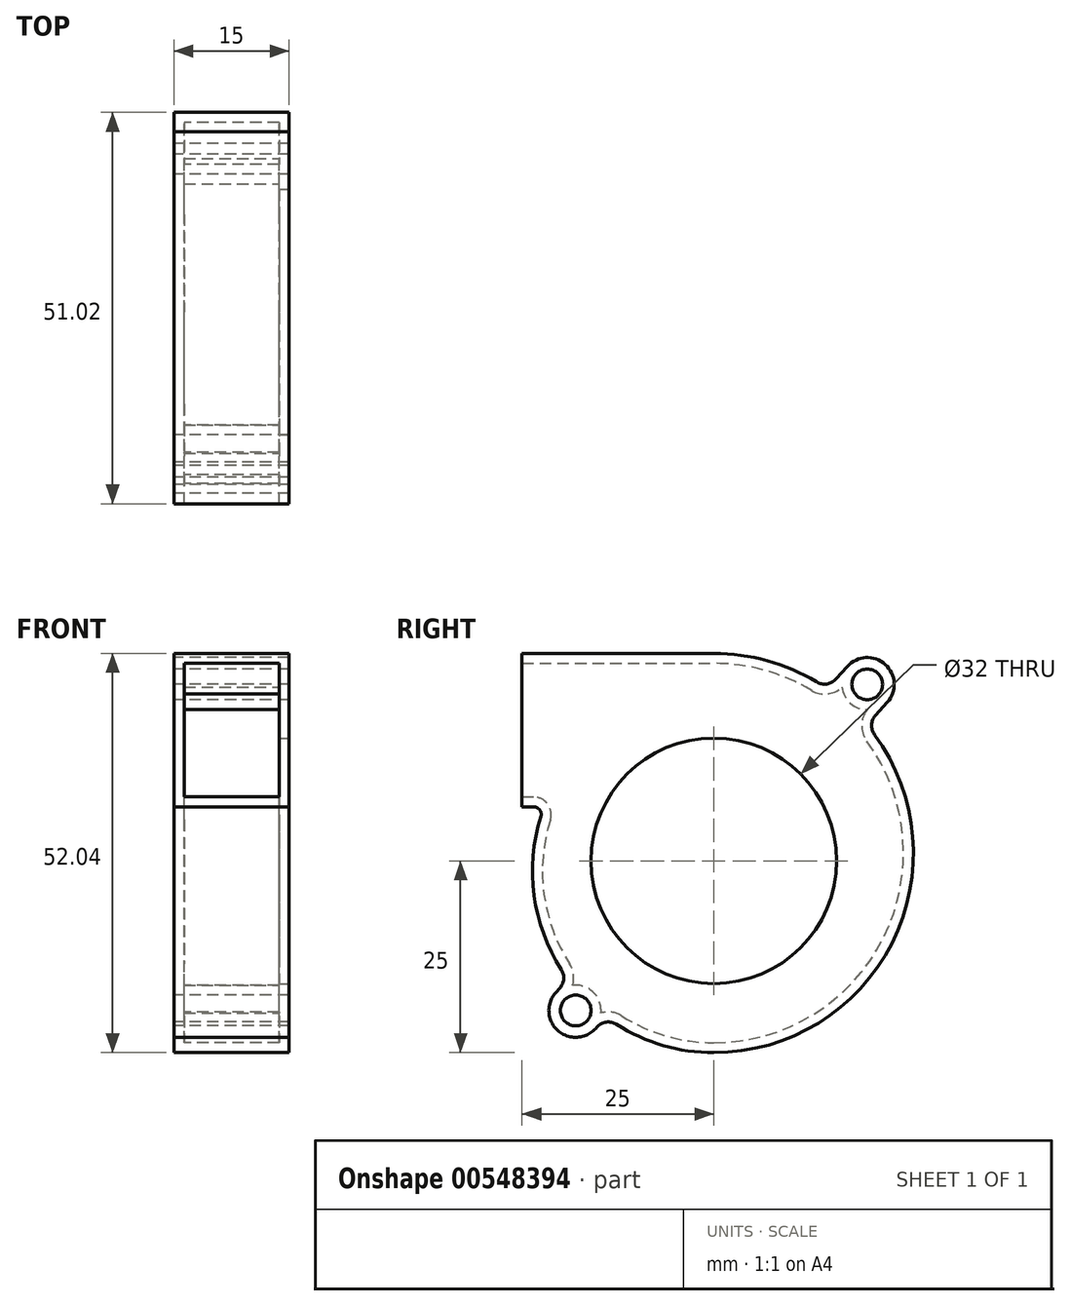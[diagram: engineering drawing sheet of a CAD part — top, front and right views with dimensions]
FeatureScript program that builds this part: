
annotation { "Feature Type Name" : "Feature", "Feature Type Description" : "" }
export const myFeature = defineFeature(function(context is Context, id is Id, definition is map)
    precondition{}
    {
        {
            var Q0;
            Q0=qCreatedBy(makeId("Right.planeOp"),FACE);
            var sketch = newSketch(context, id + "F0", { "sketchPlane" : qUnion([Q0])});
            skCircle(sketch, "E0", {"center": v(0, 0) * mm, "radius": 12 * mm});
            skCircle(sketch, "E1", {"center": v(20, 23) * mm, "radius": 2 * mm});
            skCircle(sketch, "E2", {"center": v(-18, -19.5) * mm, "radius": 2 * mm});
            skLineSegment(sketch, "E3", {"start": v(-25, 27.04) * mm, "end": v(-25, 7.04) * mm});
            skLineSegment(sketch, "E4", {"start": v(26, 45.4) * mm, "end": v(26, -37.85) * mm, "construction": true});
            skCircle(sketch, "E5", {"center": v(0, 0) * mm, "radius": 16 * mm});
            skLineSegment(sketch, "E6", {"start": v(-25, 27.04) * mm, "end": v(65.28, 27.04) * mm, "construction": true});
            skLineSegment(sketch, "E7", {"start": v(-25, 27.04) * mm, "end": v(0, 27.04) * mm});
            skArc(sketch, "E8", {"start": v(22.6, 20.66) * mm, "mid": v(22.34, 25.6) * mm, "end": v(17.4, 25.34) * mm});
            skArc(sketch, "E9", {"start": v(-20.6, -17.16) * mm, "mid": v(-20.34, -22.1) * mm, "end": v(-15.4, -21.84) * mm});
            skArc(sketch, "E10", {"start": v(26, 0) * mm, "mid": v(24.88, 8.65) * mm, "end": v(20.95, 16.45) * mm});
            skArc(sketch, "E11", {"start": v(0, -25) * mm, "mid": v(18.03, -17.74) * mm, "end": v(26, 0) * mm});
            skArc(sketch, "E12", {"start": v(-22.55, 5.74) * mm, "mid": v(-23.43, -4.5) * mm, "end": v(-19.88, -14.15) * mm});
            skLineSegment(sketch, "E13", {"start": v(-25, 7.04) * mm, "end": v(-23.5, 7.04) * mm});
            skPoint(sketch, "E14.visualSharp", {"position": v(-22.1, 7.04) * mm});
            skArc(sketch, "E14.filletArc", {"start": v(-22.55, 5.74) * mm, "mid": v(-22.7, 6.63) * mm, "end": v(-23.5, 7.04) * mm});
            skLineSegment(sketch, "E15", {"start": v(-20.6, -17.16) * mm, "end": v(-20.07, -16.57) * mm});
            skLineSegment(sketch, "E16", {"start": v(-15.4, -21.84) * mm, "end": v(-15.24, -21.66) * mm});
            skLineSegment(sketch, "E17", {"start": v(17.4, 25.34) * mm, "end": v(15.92, 23.7) * mm});
            skLineSegment(sketch, "E18", {"start": v(22.6, 20.66) * mm, "end": v(21.08, 18.97) * mm});
            skArc(sketch, "E19.trimOffspring", {"start": v(-12.68, -21.31) * mm, "mid": v(-6.6, -24.06) * mm, "end": v(0, -25) * mm});
            skArc(sketch, "E20.trimOffspring", {"start": v(13.4, 23.32) * mm, "mid": v(6.95, 26.1) * mm, "end": v(0, 27.04) * mm});
            skPoint(sketch, "E21.visualSharp", {"position": v(14.78, 22.44) * mm});
            skArc(sketch, "E21.filletArc", {"start": v(13.4, 23.32) * mm, "mid": v(14.73, 23.06) * mm, "end": v(15.92, 23.7) * mm});
            skPoint(sketch, "E22.visualSharp", {"position": v(19.95, 17.72) * mm});
            skArc(sketch, "E22.filletArc", {"start": v(21.08, 18.97) * mm, "mid": v(20.57, 17.73) * mm, "end": v(20.95, 16.45) * mm});
            skPoint(sketch, "E23.visualSharp", {"position": v(-19.02, -15.4) * mm});
            skArc(sketch, "E23.filletArc", {"start": v(-20.07, -16.57) * mm, "mid": v(-19.57, -15.4) * mm, "end": v(-19.88, -14.15) * mm});
            skPoint(sketch, "E24.visualSharp", {"position": v(-14.06, -20.36) * mm});
            skArc(sketch, "E24.filletArc", {"start": v(-12.68, -21.31) * mm, "mid": v(-14.02, -21.02) * mm, "end": v(-15.24, -21.66) * mm});
            skSolve(sketch);
        }
        {
            var Q0;
            Q0=makeQuery(id+"F0.imprint","IMPRINT",FACE,{"disambiguationData":[TD([[makeQuery(id+"F0.imprint","IMPRINT",EDGE,{"derivedFrom":sQuery(id+"F0.wireOp",EDGE,"E1")}),-1.0]])]});
            var Q1;
            Q1=makeQuery(id+"F0.imprint","IMPRINT",FACE,{"disambiguationData":[TD([[makeQuery(id+"F0.imprint","IMPRINT",EDGE,{"derivedFrom":sQuery(id+"F0.wireOp",EDGE,"E0")}),-1.0]])]});
            var Q2;
            Q2=makeQuery(id+"F0.imprint","IMPRINT",FACE,{"disambiguationData":[TD([[makeQuery(id+"F0.imprint","IMPRINT",EDGE,{"derivedFrom":sQuery(id+"F0.wireOp",EDGE,"E0")}),1.0]])]});
            extrude(context, id + "F1", {"entities" : qUnion([Q0, Q1, Q2]), "depth" : 15 * mm});
        }
        {
            var Q0;
            Q0=makeQuery(id+"F1.opExtrude","SWEPT_FACE",FACE,{"disambiguationData":[OSD([sQuery(id+"F0.wireOp",EDGE,"E3")])]});
            shell(context, id + "F2", {"entities" : qUnion([Q0]), "thickness" : 1.3 * mm});
        }
        {
            var Q0;
            Q0=makeQuery(id+"F1.opExtrude","CAP_FACE",FACE,{"disambiguationData":[OSD([sQuery(id+"F0.wireOp",EDGE,"E1"),sQuery(id+"F0.wireOp",EDGE,"E2"),sQuery(id+"F0.wireOp",EDGE,"E3"),sQuery(id+"F0.wireOp",EDGE,"E7"),sQuery(id+"F0.wireOp",EDGE,"E8"),sQuery(id+"F0.wireOp",EDGE,"E9"),sQuery(id+"F0.wireOp",EDGE,"E10"),sQuery(id+"F0.wireOp",EDGE,"E11"),sQuery(id+"F0.wireOp",EDGE,"E12"),sQuery(id+"F0.wireOp",EDGE,"E13"),sQuery(id+"F0.wireOp",EDGE,"E14.filletArc"),sQuery(id+"F0.wireOp",EDGE,"E15"),sQuery(id+"F0.wireOp",EDGE,"E16"),sQuery(id+"F0.wireOp",EDGE,"E17"),sQuery(id+"F0.wireOp",EDGE,"E18"),sQuery(id+"F0.wireOp",EDGE,"E19.trimOffspring"),sQuery(id+"F0.wireOp",EDGE,"E20.trimOffspring"),sQuery(id+"F0.wireOp",EDGE,"E21.filletArc"),sQuery(id+"F0.wireOp",EDGE,"E22.filletArc"),sQuery(id+"F0.wireOp",EDGE,"E23.filletArc"),sQuery(id+"F0.wireOp",EDGE,"E24.filletArc")])],"isStart":false});
            var sketch = newSketch(context, id + "F3", { "sketchPlane" : qUnion([Q0])});
            skCircle(sketch, "E25.0", {"center": v(0, 0) * mm, "radius": 16 * mm});
            skSolve(sketch);
        }
        {
            var Q0;
            Q0 = qSketchRegion(id + "F3", true);
            var Q1;
            {var subQ0=sQuery(id+"F0.wireOp",EDGE,"E24.filletArc");var subQ1=sQuery(id+"F0.wireOp",EDGE,"E23.filletArc");var subQ2=sQuery(id+"F0.wireOp",EDGE,"E22.filletArc");var subQ3=sQuery(id+"F0.wireOp",EDGE,"E21.filletArc");var subQ4=sQuery(id+"F0.wireOp",EDGE,"E20.trimOffspring");var subQ5=sQuery(id+"F0.wireOp",EDGE,"E19.trimOffspring");var subQ6=sQuery(id+"F0.wireOp",EDGE,"E18");var subQ7=sQuery(id+"F0.wireOp",EDGE,"E17");var subQ8=sQuery(id+"F0.wireOp",EDGE,"E16");var subQ9=sQuery(id+"F0.wireOp",EDGE,"E15");var subQ10=sQuery(id+"F0.wireOp",EDGE,"E14.filletArc");var subQ11=sQuery(id+"F0.wireOp",EDGE,"E13");var subQ12=sQuery(id+"F0.wireOp",EDGE,"E12");var subQ13=sQuery(id+"F0.wireOp",EDGE,"E11");var subQ14=sQuery(id+"F0.wireOp",EDGE,"E10");var subQ15=sQuery(id+"F0.wireOp",EDGE,"E9");var subQ16=sQuery(id+"F0.wireOp",EDGE,"E8");var subQ17=sQuery(id+"F0.wireOp",EDGE,"E7");var subQ18=sQuery(id+"F0.wireOp",EDGE,"E3");var subQ19=sQuery(id+"F0.wireOp",EDGE,"E2");var subQ20=sQuery(id+"F0.wireOp",EDGE,"E1");Q1=makeQuery(id+"F2.opShell","OFFSET_FACE",FACE,{"disambiguationData":[OSD([subQ20,subQ19,subQ18,subQ17,subQ16,subQ15,subQ14,subQ13,subQ12,subQ11,subQ10,subQ9,subQ8,subQ7,subQ6,subQ5,subQ4,subQ3,subQ2,subQ1,subQ0]),TDD([makeQuery(id+"F1.opExtrude","CAP_FACE",FACE,{"disambiguationData":[OSD([subQ20,subQ19,subQ18,subQ17,subQ16,subQ15,subQ14,subQ13,subQ12,subQ11,subQ10,subQ9,subQ8,subQ7,subQ6,subQ5,subQ4,subQ3,subQ2,subQ1,subQ0])],"isStart":true})])]});}
            extrude(context, id + "F4", {"entities" : qUnion([Q0]), "operationType" : NewBodyOperationType.REMOVE, "endBound" : BoundingType.UP_TO_SURFACE, "oppositeDirection" : true, "depth" : 25 * mm, "endBoundEntityFace" : qUnion([Q1]), "offsetDistance" : 25 * mm});
        }
    });
